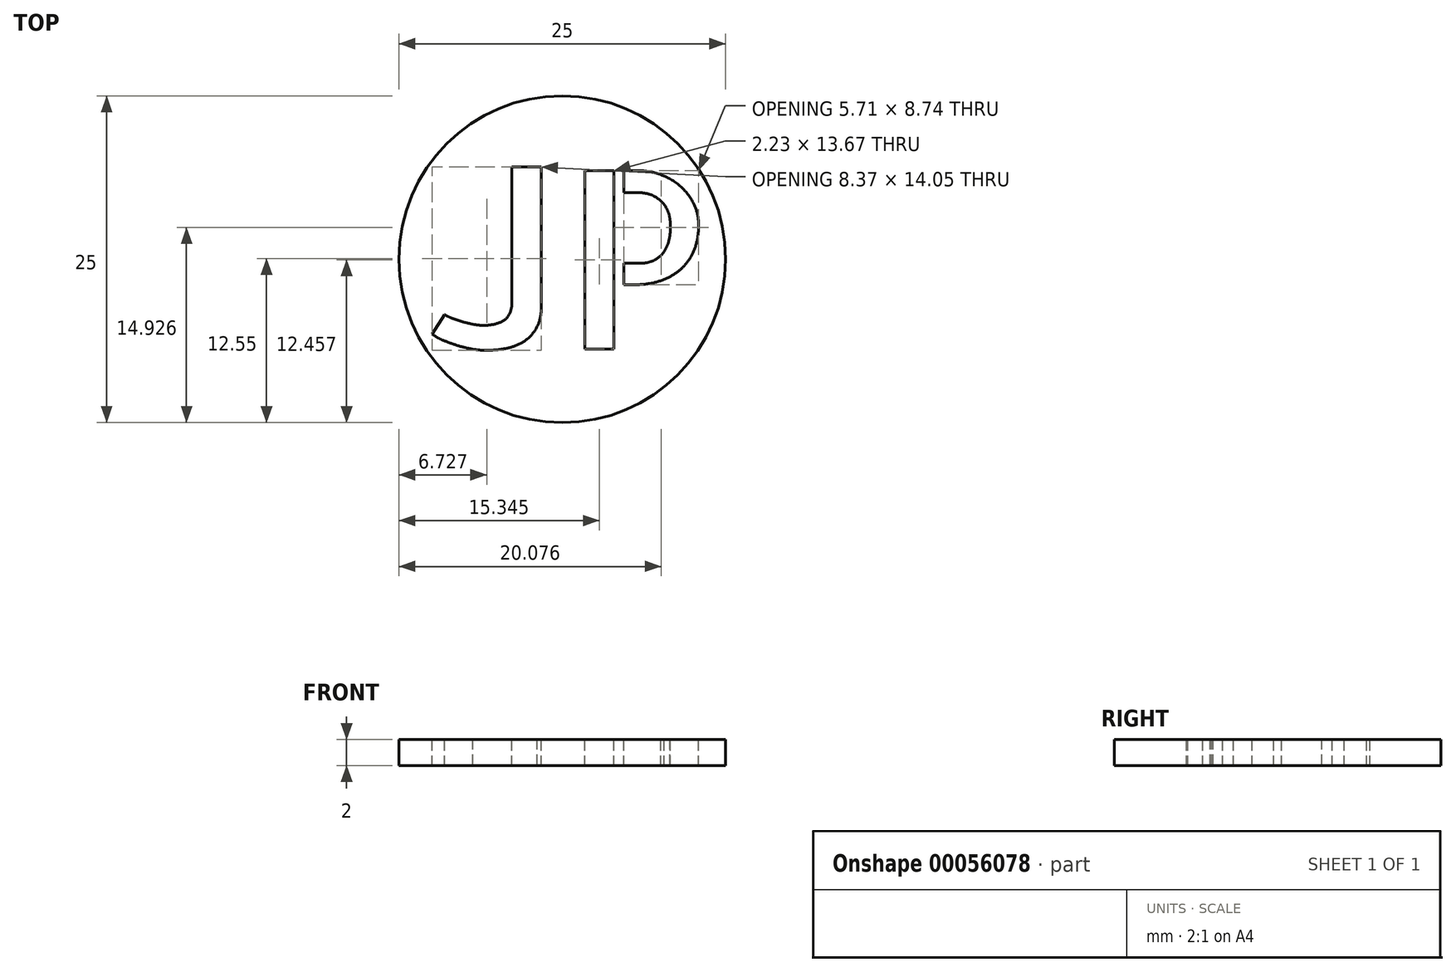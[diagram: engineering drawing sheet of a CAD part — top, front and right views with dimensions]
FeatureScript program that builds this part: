
annotation { "Feature Type Name" : "Feature", "Feature Type Description" : "" }
export const myFeature = defineFeature(function(context is Context, id is Id, definition is map)
    precondition{}
    {
        {
            var Q0;
            Q0=qCreatedBy(makeId("Top.planeOp"),FACE);
            var sketch = newSketch(context, id + "F0", { "sketchPlane" : qUnion([Q0])});
            skCircle(sketch, "E0", {"center": v(0, 0) * mm, "radius": 12.5 * mm});
            skSolve(sketch);
        }
        {
            var Q0;
            Q0 = qSketchRegion(id + "F0", true);
            extrude(context, id + "F1", {"entities" : qUnion([Q0]), "depth" : 2 * mm});
        }
        {
            var Q0;
            Q0=makeQuery(id+"F1.opExtrude","CAP_FACE",FACE,{"disambiguationData":[OSD([sQuery(id+"F0.wireOp",EDGE,"E0")])],"isStart":false});
            var sketch = newSketch(context, id + "F2", { "sketchPlane" : qUnion([Q0])});
            skText(sketch, "E1", { "text": "JP", "fontName": "AllertaStencil-Regular.ttf"});
            const initialGuessF2  = {"E1": [-0.01044, -0.00688, 1, 0, 0.01368]};
            skSetInitialGuess(sketch, initialGuessF2);
            skSolve(sketch);
        }
        {
            var Q0;
            Q0 = qSketchRegion(id + "F2", true);
            extrude(context, id + "F3", {"entities" : qUnion([Q0]), "operationType" : NewBodyOperationType.REMOVE, "oppositeDirection" : true, "depth" : 2 * mm});
        }
    });
